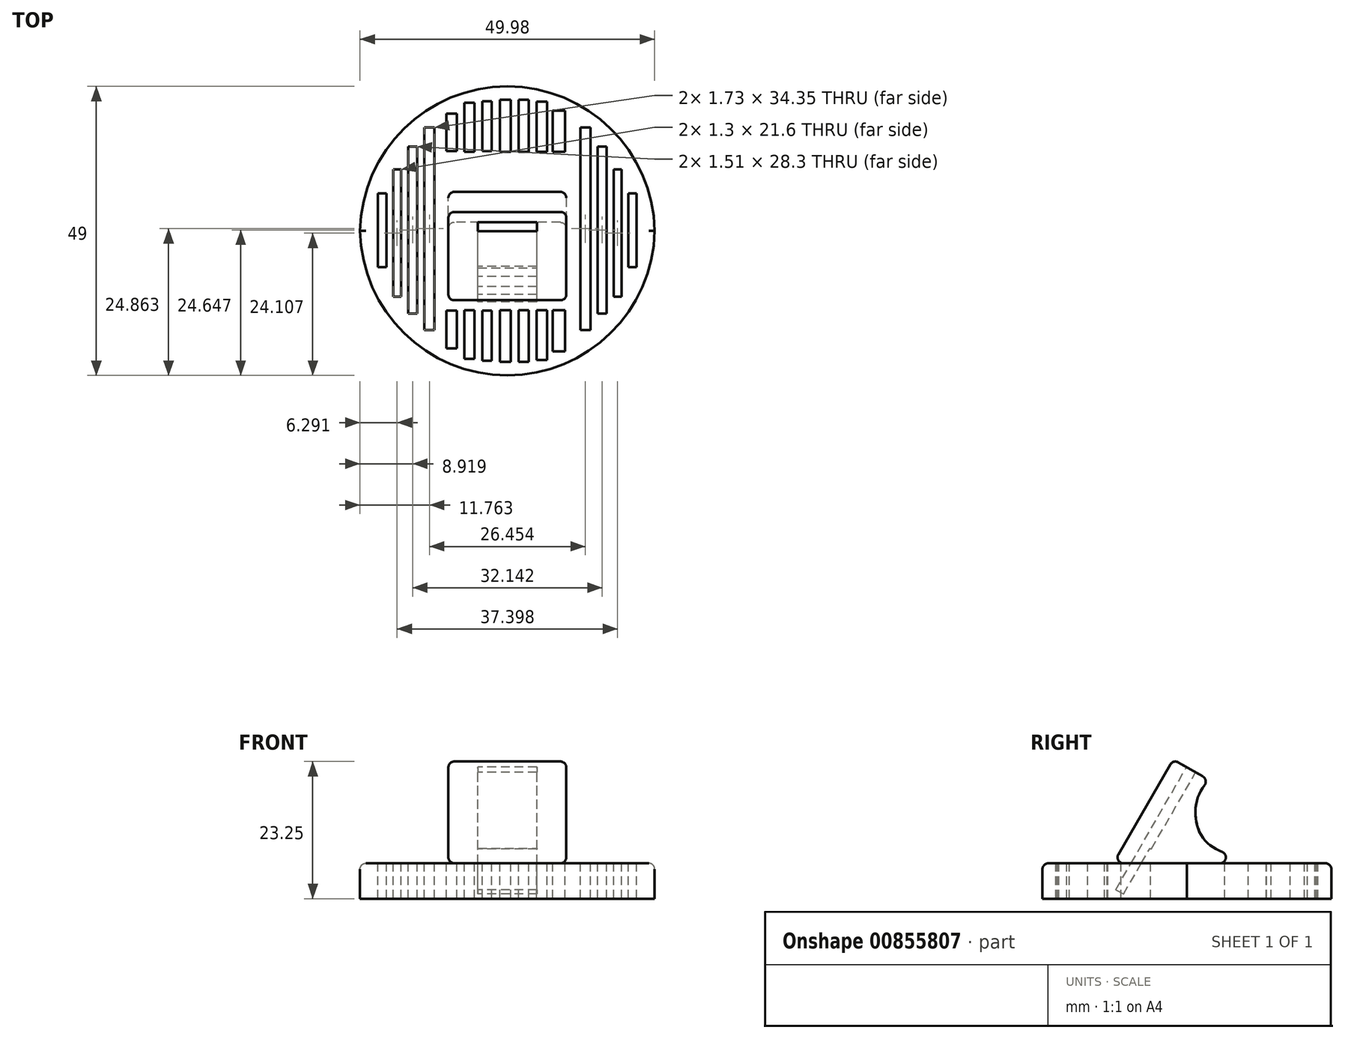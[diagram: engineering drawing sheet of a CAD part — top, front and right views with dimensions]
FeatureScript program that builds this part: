
annotation { "Feature Type Name" : "Feature", "Feature Type Description" : "" }
export const myFeature = defineFeature(function(context is Context, id is Id, definition is map)
    precondition{}
    {
        {
            var Q0;
            Q0=qCreatedBy(makeId("Right.planeOp"),FACE);
            var sketch = newSketch(context, id + "F0", { "sketchPlane" : qUnion([Q0])});
            skLineSegment(sketch, "E0.bottom", {"start": v(-12.5, 3) * mm, "end": v(12.5, 3) * mm});
            skLineSegment(sketch, "E0.top", {"start": v(-12.5, -3) * mm, "end": v(12.5, -3) * mm});
            skLineSegment(sketch, "E0.left", {"start": v(-12.5, 3) * mm, "end": v(-12.5, -3) * mm});
            skLineSegment(sketch, "E0.right", {"start": v(12.5, 3) * mm, "end": v(12.5, -3) * mm});
            skPoint(sketch, "E0.middle", {"position": v(0, 0) * mm});
            skFitSpline(sketch, "E1", {"points": [v(12.5, 3) * mm, v(1.97, 8.74) * mm, v(3.77, 17.1) * mm], "startDerivative": vector(-40.02, 9.18) * mm, "endDerivative": vector(17.65, 16.82) * mm});
            skLineSegment(sketch, "E2", {"start": v(3.77, 17.1) * mm, "end": v(-2.33, 20.62) * mm});
            skLineSegment(sketch, "E3", {"start": v(3.77, 17.1) * mm, "end": v(1.08, 14.53) * mm});
            skLineSegment(sketch, "E4", {"start": v(-12.5, 3) * mm, "end": v(-2.33, 20.62) * mm});
            skLineSegment(sketch, "E5", {"start": v(-12.5, 3) * mm, "end": v(-24.5, 3) * mm});
            skLineSegment(sketch, "E6", {"start": v(-24.5, 3) * mm, "end": v(-24.5, -3) * mm});
            skLineSegment(sketch, "E7", {"start": v(-24.5, -3) * mm, "end": v(-12.5, -3) * mm});
            skLineSegment(sketch, "E8.MirrorCS", {"start": v(12.5, 3) * mm, "end": v(24.5, 3) * mm});
            skLineSegment(sketch, "E9.MirrorCS", {"start": v(24.5, -3) * mm, "end": v(12.5, -3) * mm});
            skLineSegment(sketch, "E10.MirrorCS", {"start": v(24.5, 3) * mm, "end": v(24.5, -3) * mm});
            skSolve(sketch);
        }
        {
            var Q0;
            Q0=makeQuery(id+"F0.imprint","IMPRINT",FACE,{"disambiguationData":[TD([[makeQuery(id+"F0.imprint","IMPRINT",EDGE,{"derivedFrom":sQuery(id+"F0.wireOp",EDGE,"E0.bottom")}),-1.0]])]});
            var Q1;
            Q1=makeQuery(id+"F0.imprint","IMPRINT",FACE,{"disambiguationData":[TD([[makeQuery(id+"F0.imprint","IMPRINT",EDGE,{"derivedFrom":sQuery(id+"F0.wireOp",EDGE,"E0.left")}),-1.0]])]});
            var Q2;
            Q2=makeQuery(id+"F0.imprint","IMPRINT",FACE,{"disambiguationData":[TD([[makeQuery(id+"F0.imprint","IMPRINT",EDGE,{"derivedFrom":sQuery(id+"F0.wireOp",EDGE,"E0.right")}),1.0]])]});
            extrude(context, id + "F1", {"entities" : qUnion([Q0, Q1, Q2]), "depth" : 25 * mm, "offsetDistance" : 25 * mm, "hasSecondDirection" : true, "secondDirectionOppositeDirection" : true, "secondDirectionDepth" : 25 * mm});
        }
        {
            var Q0;
            Q0=makeQuery(id+"F0.imprint","IMPRINT",FACE,{"disambiguationData":[TD([[makeQuery(id+"F0.imprint","IMPRINT",EDGE,{"derivedFrom":sQuery(id+"F0.wireOp",EDGE,"E0.bottom")}),1.0]])]});
            extrude(context, id + "F2", {"entities" : qUnion([Q0]), "depth" : 10 * mm, "offsetDistance" : 25 * mm, "hasSecondDirection" : true, "secondDirectionOppositeDirection" : true, "secondDirectionDepth" : 10 * mm});
        }
        {
            var Q0;
            Q0=makeQuery(id+"F1.opExtrude","CAP_EDGE",EDGE,{"disambiguationData":[OSD([sQuery(id+"F0.wireOp",EDGE,"E6")])],"isStart":true});
            var Q1;
            Q1=makeQuery(id+"F1.opExtrude","CAP_EDGE",EDGE,{"disambiguationData":[OSD([sQuery(id+"F0.wireOp",EDGE,"E6")])],"isStart":false});
            var Q2;
            Q2=makeQuery(id+"F1.opExtrude","CAP_EDGE",EDGE,{"disambiguationData":[OSD([sQuery(id+"F0.wireOp",EDGE,"E10.MirrorCS")])],"isStart":true});
            var Q3;
            Q3=makeQuery(id+"F1.opExtrude","CAP_EDGE",EDGE,{"disambiguationData":[OSD([sQuery(id+"F0.wireOp",EDGE,"E10.MirrorCS")])],"isStart":false});
            fillet(context, id + "F3", {"entities" : qUnion([Q0, Q1, Q2, Q3]), "radius" : 25 * mm, "tangentPropagation" : true, "allowEdgeOverflow" : false});
        }
        {
            var Q0;
            Q0=makeQuery(id+"F3.opFillet","BLEND_EDGE",EDGE,{"blendedFrom":[makeQuery(id+"F1.opExtrude","CAP_EDGE",EDGE,{"disambiguationData":[OSD([sQuery(id+"F0.wireOp",EDGE,"E6")])],"isStart":true}),makeQuery(id+"F1.opExtrude","SWEPT_FACE",FACE,{"disambiguationData":[OSD([sQuery(id+"F0.wireOp",EDGE,"E0.bottom"),sQuery(id+"F0.wireOp",EDGE,"E5"),sQuery(id+"F0.wireOp",EDGE,"E8.MirrorCS")])]})],"blendedInto":[makeQuery(id+"F1.opExtrude","SWEPT_FACE",FACE,{"disambiguationData":[OSD([sQuery(id+"F0.wireOp",EDGE,"E0.bottom"),sQuery(id+"F0.wireOp",EDGE,"E5"),sQuery(id+"F0.wireOp",EDGE,"E8.MirrorCS")])]})]});
            var Q1;
            Q1=makeQuery(id+"F3.opFillet","BLEND_EDGE",EDGE,{"blendedFrom":[makeQuery(id+"F1.opExtrude","CAP_EDGE",EDGE,{"disambiguationData":[OSD([sQuery(id+"F0.wireOp",EDGE,"E10.MirrorCS")])],"isStart":true}),makeQuery(id+"F1.opExtrude","SWEPT_FACE",FACE,{"disambiguationData":[OSD([sQuery(id+"F0.wireOp",EDGE,"E0.bottom"),sQuery(id+"F0.wireOp",EDGE,"E5"),sQuery(id+"F0.wireOp",EDGE,"E8.MirrorCS")])]})],"blendedInto":[makeQuery(id+"F1.opExtrude","SWEPT_FACE",FACE,{"disambiguationData":[OSD([sQuery(id+"F0.wireOp",EDGE,"E0.bottom"),sQuery(id+"F0.wireOp",EDGE,"E5"),sQuery(id+"F0.wireOp",EDGE,"E8.MirrorCS")])]})]});
            var Q2;
            Q2=makeQuery(id+"F2.opExtrude","SWEPT_EDGE",EDGE,{"disambiguationData":[OSD([sQuery(id+"F0.wireOp",EDGE,"E0.bottom"),sQuery(id+"F0.wireOp",EDGE,"E0.right"),sQuery(id+"F0.wireOp",EDGE,"E1"),sQuery(id+"F0.wireOp",EDGE,"E8.MirrorCS")])]});
            var Q3;
            Q3=makeQuery(id+"F2.opExtrude","CAP_EDGE",EDGE,{"disambiguationData":[OSD([sQuery(id+"F0.wireOp",EDGE,"E0.bottom")])],"isStart":false});
            var Q4;
            Q4=makeQuery(id+"F2.opExtrude","CAP_EDGE",EDGE,{"disambiguationData":[OSD([sQuery(id+"F0.wireOp",EDGE,"E1")])],"isStart":false});
            var Q5;
            Q5=makeQuery(id+"F2.opExtrude","SWEPT_EDGE",EDGE,{"disambiguationData":[OSD([sQuery(id+"F0.wireOp",EDGE,"E1"),sQuery(id+"F0.wireOp",EDGE,"E2")])]});
            var Q6;
            Q6=makeQuery(id+"F2.opExtrude","CAP_EDGE",EDGE,{"disambiguationData":[OSD([sQuery(id+"F0.wireOp",EDGE,"E2")])],"isStart":false});
            var Q7;
            Q7=makeQuery(id+"F2.opExtrude","CAP_EDGE",EDGE,{"disambiguationData":[OSD([sQuery(id+"F0.wireOp",EDGE,"E4")])],"isStart":false});
            var Q8;
            Q8=makeQuery(id+"F2.opExtrude","CAP_EDGE",EDGE,{"disambiguationData":[OSD([sQuery(id+"F0.wireOp",EDGE,"E4")])],"isStart":true});
            var Q9;
            Q9=makeQuery(id+"F2.opExtrude","SWEPT_EDGE",EDGE,{"disambiguationData":[OSD([sQuery(id+"F0.wireOp",EDGE,"E0.bottom"),sQuery(id+"F0.wireOp",EDGE,"E0.left"),sQuery(id+"F0.wireOp",EDGE,"E4"),sQuery(id+"F0.wireOp",EDGE,"E5")])]});
            var Q10;
            Q10=makeQuery(id+"F2.opExtrude","SWEPT_EDGE",EDGE,{"disambiguationData":[OSD([sQuery(id+"F0.wireOp",EDGE,"E2"),sQuery(id+"F0.wireOp",EDGE,"E4")])]});
            var Q11;
            Q11=makeQuery(id+"F2.opExtrude","CAP_EDGE",EDGE,{"disambiguationData":[OSD([sQuery(id+"F0.wireOp",EDGE,"E2")])],"isStart":true});
            var Q12;
            Q12=makeQuery(id+"F2.opExtrude","CAP_EDGE",EDGE,{"disambiguationData":[OSD([sQuery(id+"F0.wireOp",EDGE,"E0.bottom")])],"isStart":true});
            var Q13;
            Q13=makeQuery(id+"F2.opExtrude","CAP_EDGE",EDGE,{"disambiguationData":[OSD([sQuery(id+"F0.wireOp",EDGE,"E1")])],"isStart":true});
            fillet(context, id + "F4", {"entities" : qUnion([Q0, Q1, Q2, Q3, Q4, Q5, Q6, Q7, Q8, Q9, Q10, Q11, Q12, Q13]), "radius" : 1 * mm, "tangentPropagation" : true, "allowEdgeOverflow" : false});
        }
        {
            var Q0;
            Q0=makeQuery(id+"F2.opExtrude","SWEPT_FACE",FACE,{"disambiguationData":[OSD([sQuery(id+"F0.wireOp",EDGE,"E2")])]});
            var sketch = newSketch(context, id + "F5", { "sketchPlane" : qUnion([Q0])});
            skLineSegment(sketch, "E11.bottom", {"start": v(-10, -5.91) * mm, "end": v(-10, -12) * mm});
            skLineSegment(sketch, "E11.top", {"start": v(10, -5.91) * mm, "end": v(10, -12) * mm});
            skLineSegment(sketch, "E11.left", {"start": v(-10, -5.91) * mm, "end": v(10, -5.91) * mm});
            skLineSegment(sketch, "E11.right", {"start": v(-10, -12) * mm, "end": v(10, -12) * mm});
            skLineSegment(sketch, "E12", {"start": v(-10, -12) * mm, "end": v(10, -5.91) * mm});
            skLineSegment(sketch, "E13.bottom", {"start": v(5, -9.7) * mm, "end": v(5, -8.2) * mm});
            skLineSegment(sketch, "E13.top", {"start": v(-5, -9.7) * mm, "end": v(-5, -8.2) * mm});
            skLineSegment(sketch, "E13.left", {"start": v(5, -9.7) * mm, "end": v(-5, -9.7) * mm});
            skLineSegment(sketch, "E13.right", {"start": v(5, -8.2) * mm, "end": v(-5, -8.2) * mm});
            skPoint(sketch, "E13.middle", {"position": v(0, -8.96) * mm});
            skSolve(sketch);
        }
        {
            var Q0;
            {var subQ5=sQuery(id+"F5.wireOp",EDGE,"E13.top");Q0=makeQuery(id+"F5.imprint","IMPRINT",FACE,{"disambiguationData":[TD([[makeQuery(id+"F5.imprint","IMPRINT",EDGE,{"derivedFrom":subQ5}),-1.0]])]});}
            var Q1;
            {var subQ5=sQuery(id+"F5.wireOp",EDGE,"E13.bottom");Q1=makeQuery(id+"F5.imprint","IMPRINT",FACE,{"disambiguationData":[TD([[makeQuery(id+"F5.imprint","IMPRINT",EDGE,{"derivedFrom":subQ5}),1.0]])]});}
            extrude(context, id + "F6", {"entities" : qUnion([Q0, Q1]), "operationType" : NewBodyOperationType.REMOVE, "oppositeDirection" : true, "depth" : 24 * mm, "offsetDistance" : 25 * mm});
        }
        {
            var Q0;
            Q0=makeQuery(id+"F1.opExtrude","SWEPT_FACE",FACE,{"disambiguationData":[OSD([sQuery(id+"F0.wireOp",EDGE,"E0.bottom"),sQuery(id+"F0.wireOp",EDGE,"E5"),sQuery(id+"F0.wireOp",EDGE,"E8.MirrorCS")])]});
            var sketch = newSketch(context, id + "F7", { "sketchPlane" : qUnion([Q0])});
            skLineSegment(sketch, "E14.bottom", {"start": v(-19.35, 10.4) * mm, "end": v(-18.05, 10.4) * mm});
            skLineSegment(sketch, "E14.top", {"start": v(-19.35, -11.2) * mm, "end": v(-18.05, -11.2) * mm});
            skLineSegment(sketch, "E14.left", {"start": v(-19.35, 10.4) * mm, "end": v(-19.35, -11.2) * mm});
            skLineSegment(sketch, "E14.right", {"start": v(-18.05, 10.4) * mm, "end": v(-18.05, -11.2) * mm});
            skLineSegment(sketch, "E15.bottom", {"start": v(-16.83, 14.3) * mm, "end": v(-15.32, 14.3) * mm});
            skLineSegment(sketch, "E15.top", {"start": v(-16.83, -14) * mm, "end": v(-15.32, -14) * mm});
            skLineSegment(sketch, "E15.left", {"start": v(-16.83, 14.3) * mm, "end": v(-16.83, -14) * mm});
            skLineSegment(sketch, "E15.right", {"start": v(-15.32, 14.3) * mm, "end": v(-15.32, -14) * mm});
            skLineSegment(sketch, "E16.bottom", {"start": v(-14.1, 17.54) * mm, "end": v(-12.36, 17.54) * mm});
            skLineSegment(sketch, "E16.top", {"start": v(-14.1, -16.8) * mm, "end": v(-12.36, -16.8) * mm});
            skLineSegment(sketch, "E16.left", {"start": v(-14.1, 17.54) * mm, "end": v(-14.1, -16.8) * mm});
            skLineSegment(sketch, "E16.right", {"start": v(-12.36, 17.54) * mm, "end": v(-12.36, -16.8) * mm});
            skLineSegment(sketch, "E17.bottom", {"start": v(-21.94, 6.38) * mm, "end": v(-20.5, 6.38) * mm});
            skLineSegment(sketch, "E17.top", {"start": v(-21.94, -6.15) * mm, "end": v(-20.5, -6.15) * mm});
            skLineSegment(sketch, "E17.left", {"start": v(-21.94, 6.38) * mm, "end": v(-21.94, -6.15) * mm});
            skLineSegment(sketch, "E17.right", {"start": v(-20.5, 6.38) * mm, "end": v(-20.5, -6.15) * mm});
            skLineSegment(sketch, "E18.bottom", {"start": v(-10.35, 19.91) * mm, "end": v(-8.55, 19.91) * mm});
            skLineSegment(sketch, "E18.top", {"start": v(-10.35, 13.5) * mm, "end": v(-8.55, 13.5) * mm});
            skLineSegment(sketch, "E18.left", {"start": v(-10.35, 19.91) * mm, "end": v(-10.35, 13.5) * mm});
            skLineSegment(sketch, "E18.right", {"start": v(-8.55, 19.91) * mm, "end": v(-8.55, 13.5) * mm});
            skLineSegment(sketch, "E19.bottom", {"start": v(-7.32, 21.71) * mm, "end": v(-5.6, 21.71) * mm});
            skLineSegment(sketch, "E19.top", {"start": v(-7.32, 13.43) * mm, "end": v(-5.6, 13.43) * mm});
            skLineSegment(sketch, "E19.left", {"start": v(-7.32, 21.71) * mm, "end": v(-7.32, 13.43) * mm});
            skLineSegment(sketch, "E19.right", {"start": v(-5.6, 21.71) * mm, "end": v(-5.6, 13.43) * mm});
            skLineSegment(sketch, "E20.bottom", {"start": v(-4.23, 22) * mm, "end": v(-2.64, 22) * mm});
            skLineSegment(sketch, "E20.top", {"start": v(-4.23, 13.5) * mm, "end": v(-2.64, 13.5) * mm});
            skLineSegment(sketch, "E20.left", {"start": v(-4.23, 22) * mm, "end": v(-4.23, 13.5) * mm});
            skLineSegment(sketch, "E20.right", {"start": v(-2.64, 22) * mm, "end": v(-2.64, 13.5) * mm});
            skLineSegment(sketch, "E21.bottom", {"start": v(-1.27, 22.22) * mm, "end": v(0.6, 22.22) * mm});
            skLineSegment(sketch, "E21.top", {"start": v(-1.27, 13.43) * mm, "end": v(0.6, 13.43) * mm});
            skLineSegment(sketch, "E21.left", {"start": v(-1.27, 22.22) * mm, "end": v(-1.27, 13.43) * mm});
            skLineSegment(sketch, "E21.right", {"start": v(0.6, 22.22) * mm, "end": v(0.6, 13.43) * mm});
            skLineSegment(sketch, "E22.bottom", {"start": v(1.9, 22.22) * mm, "end": v(3.62, 22.22) * mm});
            skLineSegment(sketch, "E22.top", {"start": v(1.9, 13.43) * mm, "end": v(3.62, 13.43) * mm});
            skLineSegment(sketch, "E22.left", {"start": v(1.9, 22.22) * mm, "end": v(1.9, 13.43) * mm});
            skLineSegment(sketch, "E22.right", {"start": v(3.62, 22.22) * mm, "end": v(3.62, 13.43) * mm});
            skLineSegment(sketch, "E23.bottom", {"start": v(4.99, 21.93) * mm, "end": v(6.72, 21.93) * mm});
            skLineSegment(sketch, "E23.top", {"start": v(4.99, 13.43) * mm, "end": v(6.72, 13.43) * mm});
            skLineSegment(sketch, "E23.left", {"start": v(4.99, 21.93) * mm, "end": v(4.99, 13.43) * mm});
            skLineSegment(sketch, "E23.right", {"start": v(6.72, 21.93) * mm, "end": v(6.72, 13.43) * mm});
            skLineSegment(sketch, "E24.bottom", {"start": v(7.73, 20.42) * mm, "end": v(9.81, 20.42) * mm});
            skLineSegment(sketch, "E24.top", {"start": v(7.73, 13.43) * mm, "end": v(9.81, 13.43) * mm});
            skLineSegment(sketch, "E24.left", {"start": v(7.73, 20.42) * mm, "end": v(7.73, 13.43) * mm});
            skLineSegment(sketch, "E24.right", {"start": v(9.81, 20.42) * mm, "end": v(9.81, 13.43) * mm});
            skLineSegment(sketch, "E25.MirrorCS", {"start": v(4.99, -13.43) * mm, "end": v(6.72, -13.43) * mm});
            skLineSegment(sketch, "E26.MirrorCS", {"start": v(-7.32, -13.43) * mm, "end": v(-5.6, -13.43) * mm});
            skLineSegment(sketch, "E27.MirrorCS", {"start": v(-4.23, -13.5) * mm, "end": v(-2.64, -13.5) * mm});
            skLineSegment(sketch, "E28.MirrorCS", {"start": v(-1.27, -22.22) * mm, "end": v(0.6, -22.22) * mm});
            skLineSegment(sketch, "E29.MirrorCS", {"start": v(1.9, -13.43) * mm, "end": v(3.62, -13.43) * mm});
            skLineSegment(sketch, "E30.MirrorCS", {"start": v(1.9, -22.22) * mm, "end": v(3.62, -22.22) * mm});
            skLineSegment(sketch, "E31.MirrorCS", {"start": v(4.99, -21.93) * mm, "end": v(6.72, -21.93) * mm});
            skLineSegment(sketch, "E32.MirrorCS", {"start": v(-4.23, -22) * mm, "end": v(-2.64, -22) * mm});
            skLineSegment(sketch, "E33.MirrorCS", {"start": v(-7.32, -21.71) * mm, "end": v(-5.6, -21.71) * mm});
            skLineSegment(sketch, "E34.MirrorCS", {"start": v(-1.27, -13.43) * mm, "end": v(0.6, -13.43) * mm});
            skLineSegment(sketch, "E35.MirrorCS", {"start": v(-10.35, -19.91) * mm, "end": v(-10.35, -13.5) * mm});
            skLineSegment(sketch, "E36.MirrorCS", {"start": v(1.9, -22.22) * mm, "end": v(1.9, -13.43) * mm});
            skLineSegment(sketch, "E37.MirrorCS", {"start": v(-4.23, -22) * mm, "end": v(-4.23, -13.5) * mm});
            skLineSegment(sketch, "E38.MirrorCS", {"start": v(6.72, -21.93) * mm, "end": v(6.72, -13.43) * mm});
            skLineSegment(sketch, "E39.MirrorCS", {"start": v(7.73, -20.42) * mm, "end": v(9.81, -20.42) * mm});
            skLineSegment(sketch, "E40.MirrorCS", {"start": v(-2.64, -22) * mm, "end": v(-2.64, -13.5) * mm});
            skLineSegment(sketch, "E41.MirrorCS", {"start": v(3.62, -22.22) * mm, "end": v(3.62, -13.43) * mm});
            skLineSegment(sketch, "E42.MirrorCS", {"start": v(4.99, -21.93) * mm, "end": v(4.99, -13.43) * mm});
            skLineSegment(sketch, "E43.MirrorCS", {"start": v(0.6, -22.22) * mm, "end": v(0.6, -13.43) * mm});
            skLineSegment(sketch, "E44.MirrorCS", {"start": v(7.73, -13.43) * mm, "end": v(9.81, -13.43) * mm});
            skLineSegment(sketch, "E45.MirrorCS", {"start": v(-8.55, -19.91) * mm, "end": v(-8.55, -13.5) * mm});
            skLineSegment(sketch, "E46.MirrorCS", {"start": v(-1.27, -22.22) * mm, "end": v(-1.27, -13.43) * mm});
            skLineSegment(sketch, "E47.MirrorCS", {"start": v(7.73, -20.42) * mm, "end": v(7.73, -13.43) * mm});
            skLineSegment(sketch, "E48.MirrorCS", {"start": v(-10.35, -13.5) * mm, "end": v(-8.55, -13.5) * mm});
            skLineSegment(sketch, "E49.MirrorCS", {"start": v(-5.6, -21.71) * mm, "end": v(-5.6, -13.43) * mm});
            skLineSegment(sketch, "E50.MirrorCS", {"start": v(-10.35, -19.91) * mm, "end": v(-8.55, -19.91) * mm});
            skLineSegment(sketch, "E51.MirrorCS", {"start": v(9.81, -20.42) * mm, "end": v(9.81, -13.43) * mm});
            skLineSegment(sketch, "E52.MirrorCS", {"start": v(-7.32, -21.71) * mm, "end": v(-7.32, -13.43) * mm});
            skLineSegment(sketch, "E53.MirrorCS", {"start": v(16.83, -14) * mm, "end": v(15.32, -14) * mm});
            skLineSegment(sketch, "E54.MirrorCS", {"start": v(19.35, -11.2) * mm, "end": v(18.05, -11.2) * mm});
            skLineSegment(sketch, "E55.MirrorCS", {"start": v(14.1, 17.54) * mm, "end": v(12.36, 17.54) * mm});
            skLineSegment(sketch, "E56.MirrorCS", {"start": v(14.1, -16.8) * mm, "end": v(12.36, -16.8) * mm});
            skLineSegment(sketch, "E57.MirrorCS", {"start": v(19.35, 10.4) * mm, "end": v(18.05, 10.4) * mm});
            skLineSegment(sketch, "E58.MirrorCS", {"start": v(16.83, 14.3) * mm, "end": v(15.32, 14.3) * mm});
            skLineSegment(sketch, "E59.MirrorCS", {"start": v(21.94, 6.38) * mm, "end": v(20.5, 6.38) * mm});
            skLineSegment(sketch, "E60.MirrorCS", {"start": v(21.94, -6.15) * mm, "end": v(20.5, -6.15) * mm});
            skLineSegment(sketch, "E61.MirrorCS", {"start": v(15.32, 14.3) * mm, "end": v(15.32, -14) * mm});
            skLineSegment(sketch, "E62.MirrorCS", {"start": v(16.83, 14.3) * mm, "end": v(16.83, -14) * mm});
            skLineSegment(sketch, "E63.MirrorCS", {"start": v(20.5, 6.38) * mm, "end": v(20.5, -6.15) * mm});
            skLineSegment(sketch, "E64.MirrorCS", {"start": v(18.05, 10.4) * mm, "end": v(18.05, -11.2) * mm});
            skLineSegment(sketch, "E65.MirrorCS", {"start": v(19.35, 10.4) * mm, "end": v(19.35, -11.2) * mm});
            skLineSegment(sketch, "E66.MirrorCS", {"start": v(12.36, 17.54) * mm, "end": v(12.36, -16.8) * mm});
            skLineSegment(sketch, "E67.MirrorCS", {"start": v(14.1, 17.54) * mm, "end": v(14.1, -16.8) * mm});
            skLineSegment(sketch, "E68.MirrorCS", {"start": v(21.94, 6.38) * mm, "end": v(21.94, -6.15) * mm});
            skSolve(sketch);
        }
        {
            var Q0;
            Q0 = qSketchRegion(id + "F7", true);
            extrude(context, id + "F8", {"entities" : qUnion([Q0]), "operationType" : NewBodyOperationType.REMOVE, "oppositeDirection" : true, "depth" : 25 * mm, "offsetDistance" : 25 * mm});
        }
        {
            var Q0;
            Q0=makeQuery(id+"F2.opExtrude","SWEPT_FACE",FACE,{"disambiguationData":[OSD([sQuery(id+"F0.wireOp",EDGE,"E2")])]});
            var sketch = newSketch(context, id + "F9", { "sketchPlane" : qUnion([Q0])});
            skLineSegment(sketch, "E69.bottom", {"start": v(-10, -5.63) * mm, "end": v(-10, -11.72) * mm});
            skLineSegment(sketch, "E69.top", {"start": v(10, -5.63) * mm, "end": v(10, -11.72) * mm});
            skLineSegment(sketch, "E69.left", {"start": v(-10, -5.63) * mm, "end": v(10, -5.63) * mm});
            skLineSegment(sketch, "E69.right", {"start": v(-10, -11.72) * mm, "end": v(10, -11.72) * mm});
            skLineSegment(sketch, "E70", {"start": v(-10, -11.72) * mm, "end": v(10, -5.63) * mm});
            skLineSegment(sketch, "E71.bottom", {"start": v(5, -9.43) * mm, "end": v(5, -7.93) * mm});
            skLineSegment(sketch, "E71.top", {"start": v(-5, -9.43) * mm, "end": v(-5, -7.93) * mm});
            skLineSegment(sketch, "E71.left", {"start": v(5, -9.43) * mm, "end": v(-5, -9.43) * mm});
            skLineSegment(sketch, "E71.right", {"start": v(5, -7.93) * mm, "end": v(-5, -7.93) * mm});
            skPoint(sketch, "E71.middle", {"position": v(0, -8.68) * mm});
            skSolve(sketch);
        }
        {
            var Q0;
            {var subQ5=sQuery(id+"F9.wireOp",EDGE,"E71.bottom");Q0=makeQuery(id+"F9.imprint","IMPRINT",FACE,{"disambiguationData":[TD([[makeQuery(id+"F9.imprint","IMPRINT",EDGE,{"derivedFrom":subQ5}),1.0]])]});}
            var Q1;
            {var subQ5=sQuery(id+"F9.wireOp",EDGE,"E71.top");Q1=makeQuery(id+"F9.imprint","IMPRINT",FACE,{"disambiguationData":[TD([[makeQuery(id+"F9.imprint","IMPRINT",EDGE,{"derivedFrom":subQ5}),-1.0]])]});}
            extrude(context, id + "F10", {"entities" : qUnion([Q0, Q1]), "operationType" : NewBodyOperationType.REMOVE, "oppositeDirection" : true, "depth" : 15 * mm, "offsetDistance" : 25 * mm});
        }
    });
